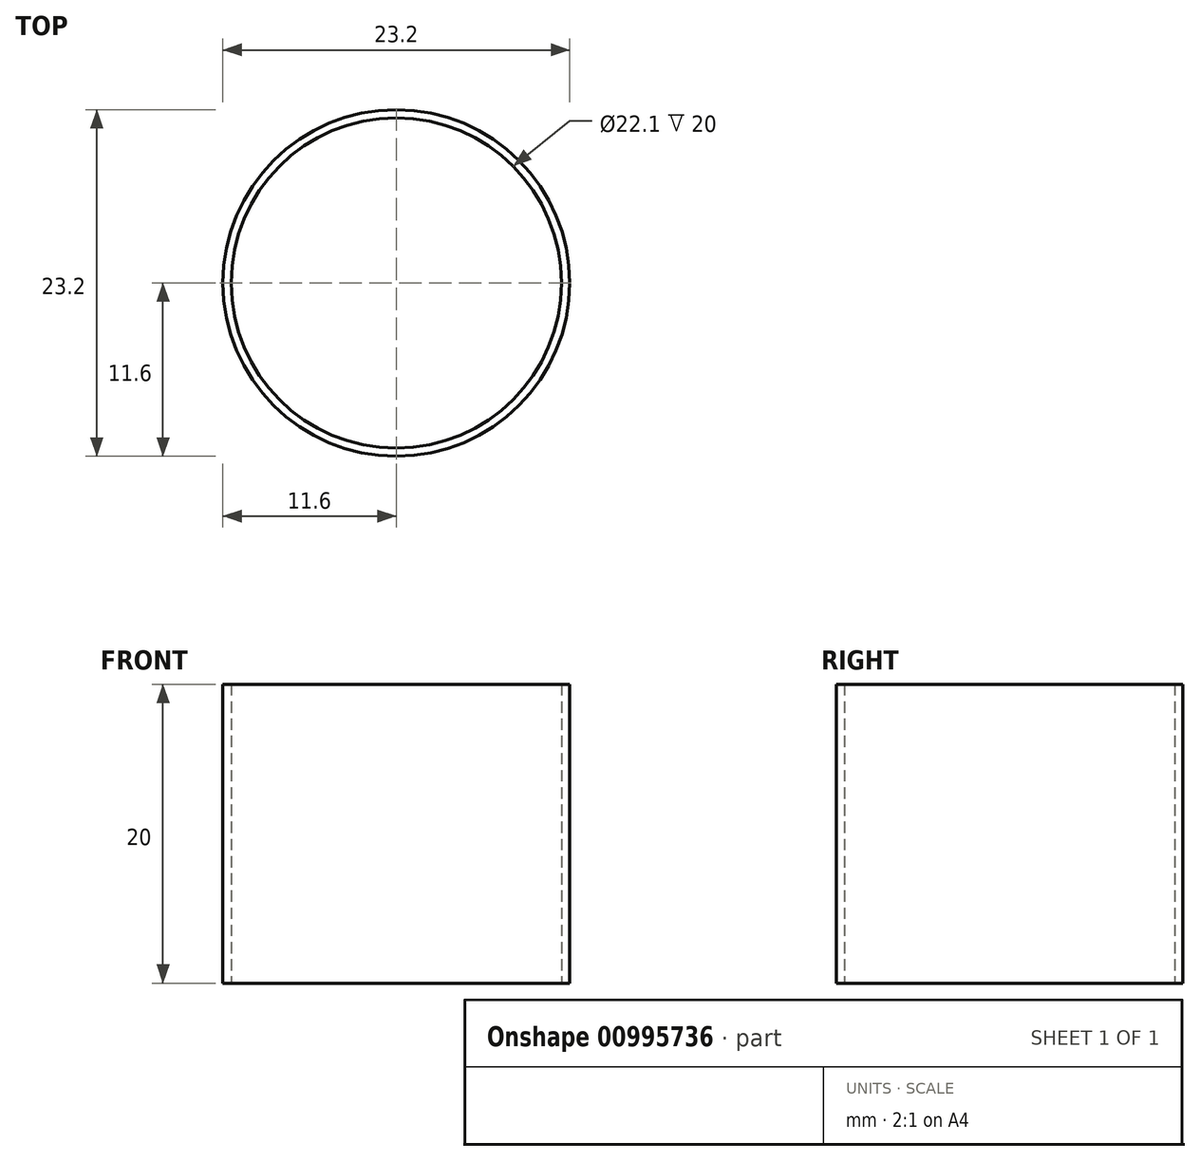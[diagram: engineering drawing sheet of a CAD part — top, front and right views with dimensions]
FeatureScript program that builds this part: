
annotation { "Feature Type Name" : "Feature", "Feature Type Description" : "" }
export const myFeature = defineFeature(function(context is Context, id is Id, definition is map)
    precondition{}
    {
        {
            var Q0;
            Q0=qCreatedBy(makeId("Top.planeOp"),FACE);
            var sketch = newSketch(context, id + "F0", { "sketchPlane" : qUnion([Q0])});
            skCircle(sketch, "E0", {"center": v(0, 0) * mm, "radius": 11.6 * mm});
            skCircle(sketch, "E1", {"center": v(0, 0) * mm, "radius": 11.05 * mm});
            skSolve(sketch);
        }
        {
            var Q0;
            Q0=makeQuery(id+"F0.imprint","IMPRINT",FACE,{"disambiguationData":[TD([[makeQuery(id+"F0.imprint","IMPRINT",EDGE,{"derivedFrom":sQuery(id+"F0.wireOp",EDGE,"E0")}),1.0]])]});
            extrude(context, id + "F1", {"entities" : qUnion([Q0]), "depth" : 20 * mm, "offsetDistance" : 25 * mm});
        }
    });
